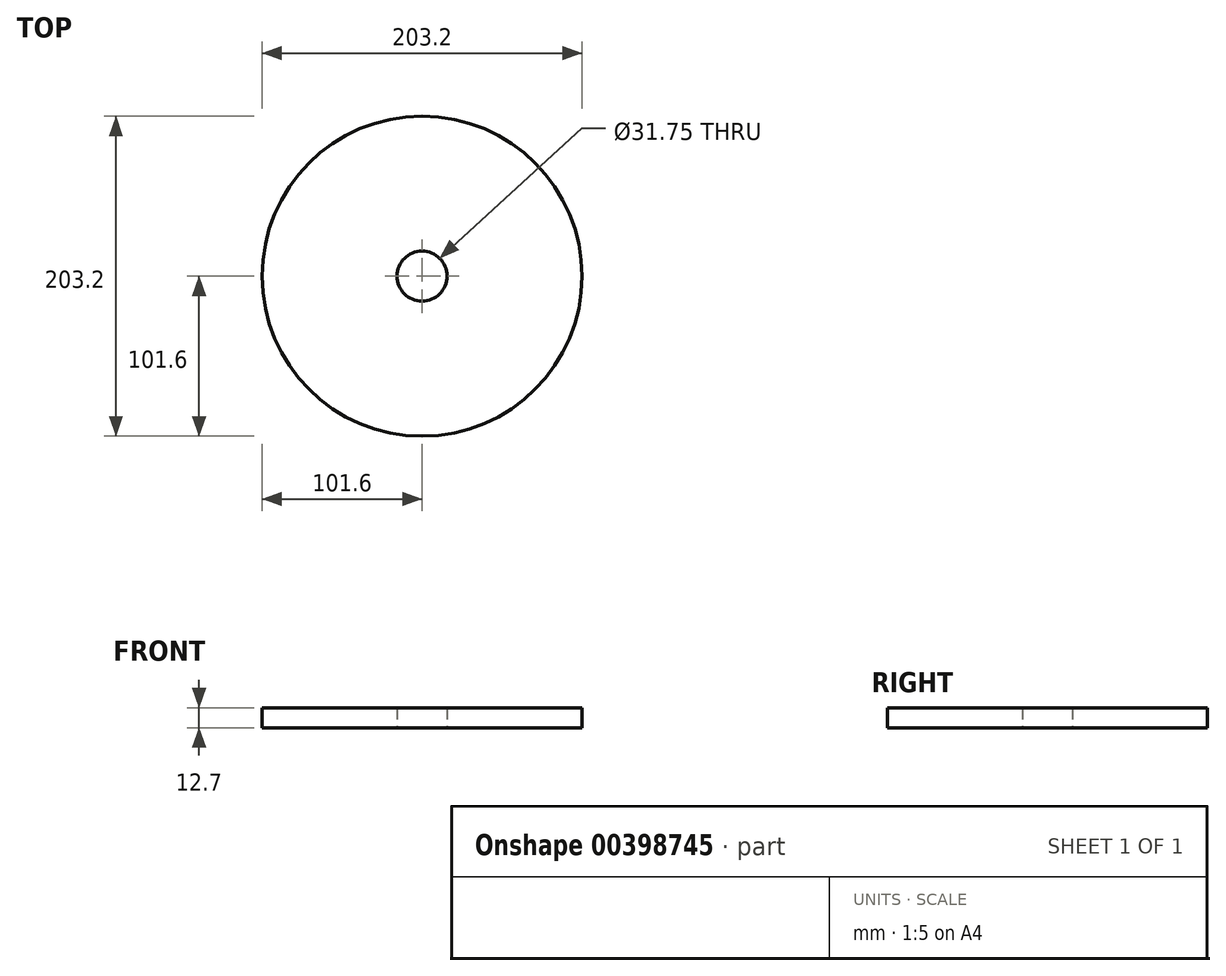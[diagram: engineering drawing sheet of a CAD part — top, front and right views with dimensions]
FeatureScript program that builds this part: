
annotation { "Feature Type Name" : "Feature", "Feature Type Description" : "" }
export const myFeature = defineFeature(function(context is Context, id is Id, definition is map)
    precondition{}
    {
        {
            var Q0;
            Q0=qCreatedBy(makeId("Top.planeOp"),FACE);
            var sketch = newSketch(context, id + "F0", { "sketchPlane" : qUnion([Q0])});
            skCircle(sketch, "E0", {"center": v(0, 0) * mm, "radius": 101.6 * mm});
            skCircle(sketch, "E1", {"center": v(0, 0) * mm, "radius": 15.88 * mm});
            skSolve(sketch);
        }
        {
            var Q0;
            Q0=makeQuery(id+"F0.imprint","IMPRINT",FACE,{"disambiguationData":[TD([[makeQuery(id+"F0.imprint","IMPRINT",EDGE,{"derivedFrom":sQuery(id+"F0.wireOp",EDGE,"E0")}),1.0]])]});
            extrude(context, id + "F1", {"entities" : qUnion([Q0]), "depth" : 12.7 * mm});
        }
    });
